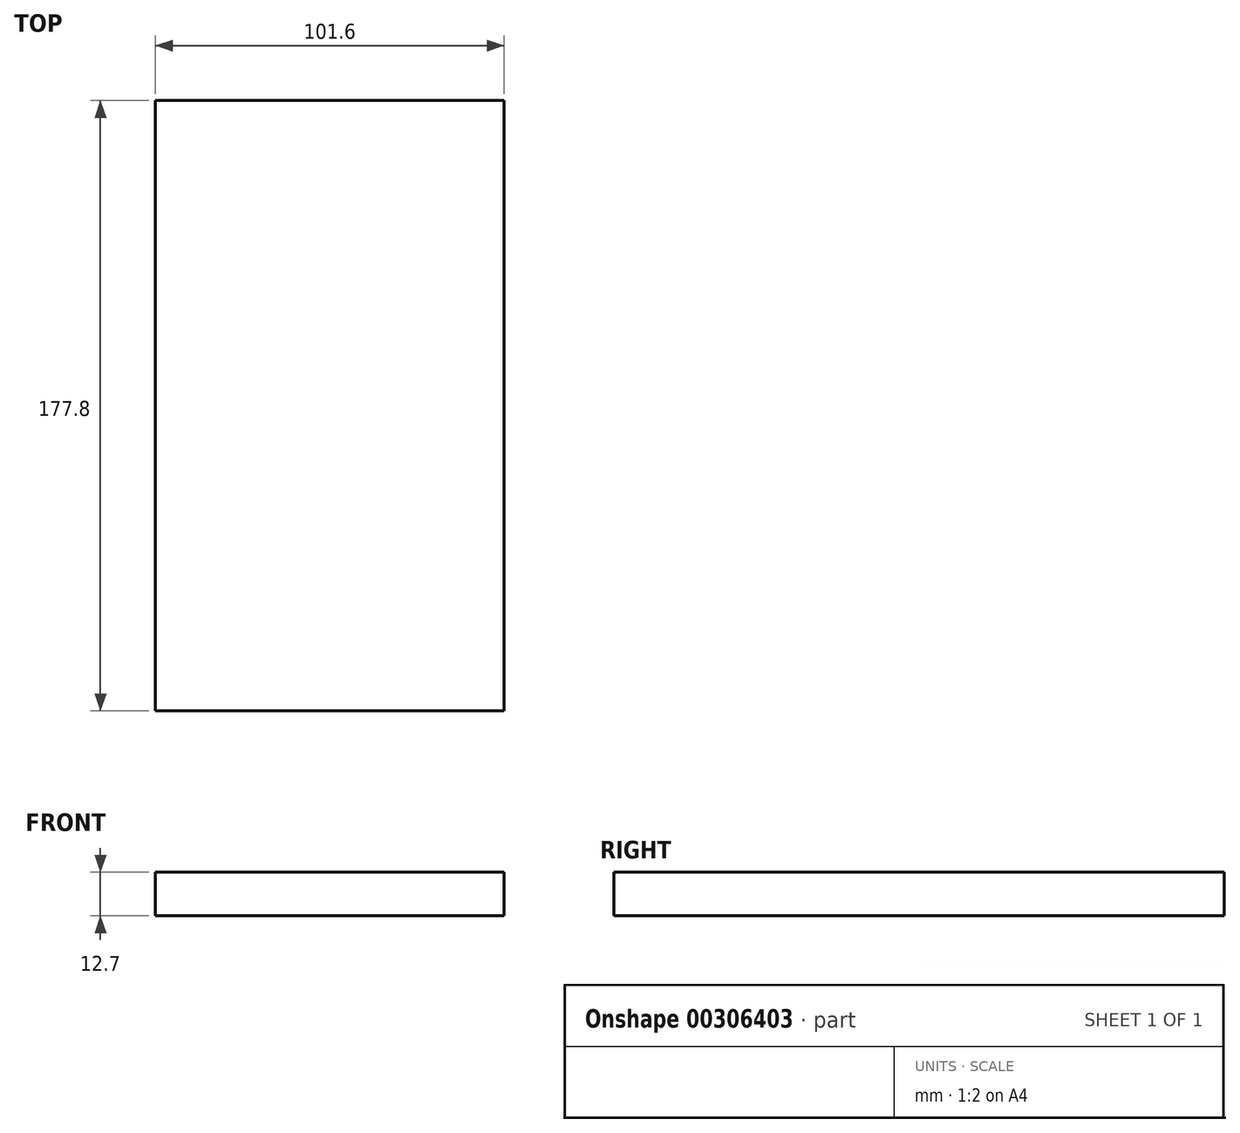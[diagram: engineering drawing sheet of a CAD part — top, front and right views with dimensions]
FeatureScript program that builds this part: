
annotation { "Feature Type Name" : "Feature", "Feature Type Description" : "" }
export const myFeature = defineFeature(function(context is Context, id is Id, definition is map)
    precondition{}
    {
        {
            var Q0;
            Q0=qCreatedBy(makeId("Top.planeOp"),FACE);
            var sketch = newSketch(context, id + "F0", { "sketchPlane" : qUnion([Q0])});
            skLineSegment(sketch, "E0.bottom", {"start": v(50.8, -88.9) * mm, "end": v(-50.8, -88.9) * mm});
            skLineSegment(sketch, "E0.top", {"start": v(50.8, 88.9) * mm, "end": v(-50.8, 88.9) * mm});
            skLineSegment(sketch, "E0.left", {"start": v(50.8, -88.9) * mm, "end": v(50.8, 88.9) * mm});
            skLineSegment(sketch, "E0.right", {"start": v(-50.8, -88.9) * mm, "end": v(-50.8, 88.9) * mm});
            skPoint(sketch, "E0.middle", {"position": v(0, 0) * mm});
            skSolve(sketch);
        }
        {
            var Q0;
            Q0 = qSketchRegion(id + "F0", true);
            extrude(context, id + "F1", {"entities" : qUnion([Q0]), "depth" : 12.7 * mm});
        }
    });
